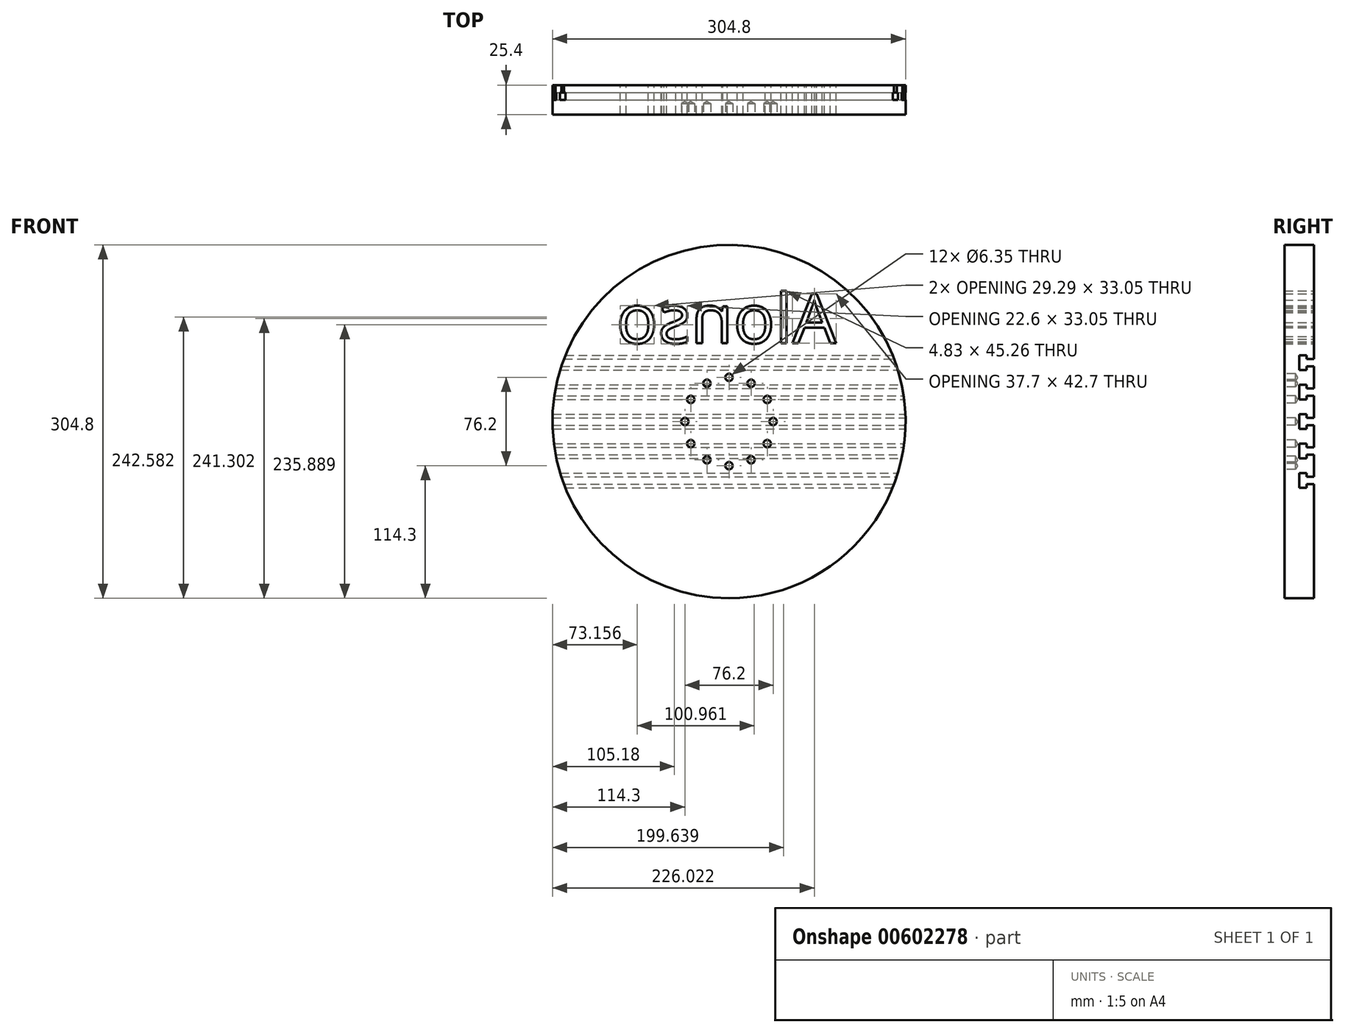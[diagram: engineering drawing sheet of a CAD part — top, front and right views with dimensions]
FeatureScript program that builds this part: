
annotation { "Feature Type Name" : "Feature", "Feature Type Description" : "" }
export const myFeature = defineFeature(function(context is Context, id is Id, definition is map)
    precondition{}
    {
        {
            var Q0;
            Q0=qCreatedBy(makeId("Front.planeOp"),FACE);
            var sketch = newSketch(context, id + "F0", { "sketchPlane" : qUnion([Q0])});
            skCircle(sketch, "E0", {"center": v(0, 0) * mm, "radius": 152.4 * mm});
            skSolve(sketch);
        }
        {
            var Q0;
            Q0 = qSketchRegion(id + "F0", true);
            extrude(context, id + "F1", {"entities" : qUnion([Q0]), "depth" : 25.4 * mm, "offsetDistance" : 25.4 * mm});
        }
        {
            var Q0;
            Q0=makeQuery(id+"F1.opExtrude","CAP_FACE",FACE,{"disambiguationData":[OSD([sQuery(id+"F0.wireOp",EDGE,"E0")])],"isStart":false});
            var sketch = newSketch(context, id + "F2", { "sketchPlane" : qUnion([Q0])});
            skCircle(sketch, "E1.0.0", {"center": v(0, 0) * mm, "radius": 152.4 * mm});
            skPoint(sketch, "E2", {"position": v(0, -38.1) * mm});
            skPoint(sketch, "E3.1.0", {"position": v(19.05, -33) * mm});
            skPoint(sketch, "E3.2.0", {"position": v(33, -19.05) * mm});
            skPoint(sketch, "E3.3.0", {"position": v(38.1, 0) * mm});
            skPoint(sketch, "E3.4.0", {"position": v(33, 19.05) * mm});
            skPoint(sketch, "E3.5.0", {"position": v(19.05, 33) * mm});
            skPoint(sketch, "E3.6.0", {"position": v(0, 38.1) * mm});
            skPoint(sketch, "E3.7.0", {"position": v(-19.05, 33) * mm});
            skPoint(sketch, "E3.8.0", {"position": v(-33, 19.05) * mm});
            skPoint(sketch, "E3.9.0", {"position": v(-38.1, 0) * mm});
            skPoint(sketch, "E3.10.0", {"position": v(-33, -19.05) * mm});
            skPoint(sketch, "E3.11.0", {"position": v(-19.05, -33) * mm});
            skSolve(sketch);
        }
        {
            var Q0;
            Q0=sQuery(id+"F2.wireOp",VERTEX,"E3.7.0");
            var Q1;
            Q1=sQuery(id+"F2.wireOp",VERTEX,"E3.6.0");
            var Q2;
            Q2=sQuery(id+"F2.wireOp",VERTEX,"E3.5.0");
            var Q3;
            Q3=sQuery(id+"F2.wireOp",VERTEX,"E3.4.0");
            var Q4;
            Q4=sQuery(id+"F2.wireOp",VERTEX,"E3.3.0");
            var Q5;
            Q5=sQuery(id+"F2.wireOp",VERTEX,"E3.2.0");
            var Q6;
            Q6=sQuery(id+"F2.wireOp",VERTEX,"E3.1.0");
            var Q7;
            Q7=sQuery(id+"F2.wireOp",VERTEX,"E2");
            var Q8;
            Q8=sQuery(id+"F2.wireOp",VERTEX,"E3.11.0");
            var Q9;
            Q9=sQuery(id+"F2.wireOp",VERTEX,"E3.10.0");
            var Q10;
            Q10=sQuery(id+"F2.wireOp",VERTEX,"E3.8.0");
            var Q11;
            Q11=sQuery(id+"F2.wireOp",VERTEX,"E3.9.0");
            var Q12;
            Q12=makeQuery(id+"F1.opExtrude","SWEPT_BODY",BODY,{"disambiguationData":[OSD([sQuery(id+"F0.wireOp",EDGE,"E0")])]});
            hole(context, id + "F3", {"style" : HoleStyle.SIMPLE, "endStyle" : HoleEndStyle.BLIND, "holeDiameter" : 6.35 * mm, "majorDiameter" : 6.35 * mm, "holeDepth" : 9.52 * mm, "isTappedThrough" : true, "tappedDepth" : 12.7 * mm, "tapClearance" : 3, "locations" : qUnion([Q0, Q1, Q2, Q3, Q4, Q5, Q6, Q7, Q8, Q9, Q10, Q11]), "scope" : qUnion([Q12])});
        }
        {
            var Q0;
            Q0=makeQuery(id+"F1.opExtrude","CAP_FACE",FACE,{"disambiguationData":[OSD([sQuery(id+"F0.wireOp",EDGE,"E0")])],"isStart":true});
            var sketch = newSketch(context, id + "F4", { "sketchPlane" : qUnion([Q0])});
            skSolve(sketch);
        }
        {
            var Q0;
            Q0=qCreatedBy(makeId("Right.planeOp"),FACE);
            cPlane(context, id + "F5", {"entities" : qUnion([Q0]), "cplaneType" : CPlaneType.OFFSET, "offset" : 152.4 * mm, "width" : 152.4 * mm, "height" : 152.4 * mm});
        }
        {
            var Q0;
            Q0=qCreatedBy(id+"F5.planeOp",FACE);
            var sketch = newSketch(context, id + "F6", { "sketchPlane" : qUnion([Q0])});
            skLineSegment(sketch, "E4.0", {"start": v(-25.4, -152.4) * mm, "end": v(-25.4, 152.4) * mm});
            skLineSegment(sketch, "E5.0", {"start": v(0, -152.4) * mm, "end": v(0, 152.4) * mm});
            skPoint(sketch, "E6", {"position": v(-25.4, 0) * mm});
            skPoint(sketch, "E7", {"position": v(0, 0) * mm});
            skPoint(sketch, "E8", {"position": v(0, 3.18) * mm});
            skPoint(sketch, "E9", {"position": v(0, -3.18) * mm});
            skPoint(sketch, "E10", {"position": v(-6.35, 3.17) * mm});
            skPoint(sketch, "E11", {"position": v(-6.35, -3.18) * mm});
            skLineSegment(sketch, "E12", {"start": v(0, 3.18) * mm, "end": v(-6.35, 3.17) * mm});
            skLineSegment(sketch, "E13", {"start": v(0, -3.18) * mm, "end": v(-6.35, -3.18) * mm});
            skPoint(sketch, "E14", {"position": v(-6.35, -6.35) * mm});
            skPoint(sketch, "E15", {"position": v(-6.35, 6.35) * mm});
            skPoint(sketch, "E16", {"position": v(-12.7, 6.35) * mm});
            skPoint(sketch, "E17", {"position": v(-12.7, -6.35) * mm});
            skLineSegment(sketch, "E18", {"start": v(-6.35, 3.17) * mm, "end": v(-6.35, 6.35) * mm});
            skLineSegment(sketch, "E19", {"start": v(-6.35, 6.35) * mm, "end": v(-12.7, 6.35) * mm});
            skLineSegment(sketch, "E20", {"start": v(-6.35, -3.18) * mm, "end": v(-6.35, -6.35) * mm});
            skLineSegment(sketch, "E21", {"start": v(-6.35, -6.35) * mm, "end": v(-12.7, -6.35) * mm});
            skLineSegment(sketch, "E22", {"start": v(-12.7, 6.35) * mm, "end": v(-12.7, -6.35) * mm});
            skPoint(sketch, "E23", {"position": v(0, 25.4) * mm});
            skPoint(sketch, "E24", {"position": v(0, 28.58) * mm});
            skPoint(sketch, "E25", {"position": v(0, 22.23) * mm});
            skPoint(sketch, "E26", {"position": v(-6.35, 28.58) * mm});
            skPoint(sketch, "E27", {"position": v(-6.35, 22.23) * mm});
            skPoint(sketch, "E28", {"position": v(-6.35, 19.05) * mm});
            skPoint(sketch, "E29", {"position": v(-6.35, 31.75) * mm});
            skPoint(sketch, "E30", {"position": v(-12.7, 19.05) * mm});
            skLineSegment(sketch, "E31", {"start": v(0, 22.23) * mm, "end": v(-6.35, 22.23) * mm});
            skLineSegment(sketch, "E32", {"start": v(-6.35, 22.23) * mm, "end": v(-6.35, 19.05) * mm});
            skLineSegment(sketch, "E33", {"start": v(-6.35, 19.05) * mm, "end": v(-12.7, 19.05) * mm});
            skLineSegment(sketch, "E34", {"start": v(-12.7, 19.05) * mm, "end": v(-12.7, 28.58) * mm});
            skLineSegment(sketch, "E35", {"start": v(0, 28.58) * mm, "end": v(-6.35, 28.58) * mm});
            skLineSegment(sketch, "E36", {"start": v(-6.35, 28.58) * mm, "end": v(-6.35, 31.75) * mm});
            skLineSegment(sketch, "E37", {"start": v(-6.35, 31.75) * mm, "end": v(-12.7, 31.75) * mm});
            skLineSegment(sketch, "E38", {"start": v(-12.7, 31.75) * mm, "end": v(-12.7, 28.58) * mm});
            skPoint(sketch, "E39", {"position": v(0, 50.8) * mm});
            skPoint(sketch, "E40", {"position": v(0, 53.98) * mm});
            skPoint(sketch, "E41", {"position": v(0, 47.63) * mm});
            skPoint(sketch, "E42", {"position": v(-6.35, 53.98) * mm});
            skPoint(sketch, "E43", {"position": v(-6.35, 47.63) * mm});
            skPoint(sketch, "E44", {"position": v(-6.35, 44.45) * mm});
            skPoint(sketch, "E45", {"position": v(-6.35, 57.15) * mm});
            skPoint(sketch, "E46", {"position": v(-12.7, 57.15) * mm});
            skPoint(sketch, "E47", {"position": v(-12.7, 44.45) * mm});
            skLineSegment(sketch, "E48", {"start": v(0, 47.63) * mm, "end": v(-6.35, 47.63) * mm});
            skLineSegment(sketch, "E49", {"start": v(-6.35, 47.63) * mm, "end": v(-6.35, 44.45) * mm});
            skLineSegment(sketch, "E50", {"start": v(-6.35, 44.45) * mm, "end": v(-12.7, 44.45) * mm});
            skLineSegment(sketch, "E51", {"start": v(-12.7, 44.45) * mm, "end": v(-12.7, 57.15) * mm});
            skLineSegment(sketch, "E52", {"start": v(-12.7, 57.15) * mm, "end": v(-6.35, 57.15) * mm});
            skLineSegment(sketch, "E53", {"start": v(-6.35, 57.15) * mm, "end": v(-6.35, 53.98) * mm});
            skLineSegment(sketch, "E54", {"start": v(-6.35, 53.98) * mm, "end": v(0, 53.98) * mm});
            skPoint(sketch, "E55", {"position": v(0, -25.4) * mm});
            skPoint(sketch, "E56", {"position": v(0, -22.23) * mm});
            skPoint(sketch, "E57", {"position": v(0, -28.58) * mm});
            skPoint(sketch, "E58", {"position": v(-6.35, -22.23) * mm});
            skPoint(sketch, "E59", {"position": v(-6.35, -28.58) * mm});
            skPoint(sketch, "E60", {"position": v(-6.35, -19.05) * mm});
            skPoint(sketch, "E61", {"position": v(-6.35, -31.75) * mm});
            skPoint(sketch, "E62", {"position": v(-12.7, -19.05) * mm});
            skPoint(sketch, "E63", {"position": v(-12.7, -31.75) * mm});
            skLineSegment(sketch, "E64", {"start": v(0, -22.23) * mm, "end": v(-6.35, -22.23) * mm});
            skLineSegment(sketch, "E65", {"start": v(-6.35, -22.23) * mm, "end": v(-6.35, -19.05) * mm});
            skLineSegment(sketch, "E66", {"start": v(-6.35, -19.05) * mm, "end": v(-12.7, -19.05) * mm});
            skLineSegment(sketch, "E67", {"start": v(-12.7, -19.05) * mm, "end": v(-12.7, -31.75) * mm});
            skLineSegment(sketch, "E68", {"start": v(-12.7, -31.75) * mm, "end": v(-6.35, -31.75) * mm});
            skLineSegment(sketch, "E69", {"start": v(-6.35, -31.75) * mm, "end": v(-6.35, -28.58) * mm});
            skLineSegment(sketch, "E70", {"start": v(-6.35, -28.58) * mm, "end": v(0, -28.58) * mm});
            skPoint(sketch, "E71", {"position": v(0, -50.8) * mm});
            skPoint(sketch, "E72", {"position": v(0, -47.63) * mm});
            skPoint(sketch, "E73", {"position": v(0, -53.98) * mm});
            skPoint(sketch, "E74", {"position": v(-6.35, -47.63) * mm});
            skPoint(sketch, "E75", {"position": v(-6.35, -53.98) * mm});
            skPoint(sketch, "E76", {"position": v(-6.35, -44.45) * mm});
            skPoint(sketch, "E77", {"position": v(-6.35, -57.15) * mm});
            skPoint(sketch, "E78", {"position": v(-12.7, -44.45) * mm});
            skPoint(sketch, "E79", {"position": v(-12.7, -57.15) * mm});
            skLineSegment(sketch, "E80", {"start": v(0, -47.63) * mm, "end": v(-6.35, -47.63) * mm});
            skLineSegment(sketch, "E81", {"start": v(-6.35, -47.63) * mm, "end": v(-6.35, -44.45) * mm});
            skLineSegment(sketch, "E82", {"start": v(-6.35, -44.45) * mm, "end": v(-12.7, -44.45) * mm});
            skLineSegment(sketch, "E83", {"start": v(-12.7, -44.45) * mm, "end": v(-12.7, -57.15) * mm});
            skLineSegment(sketch, "E84", {"start": v(-12.7, -57.15) * mm, "end": v(-6.35, -57.15) * mm});
            skLineSegment(sketch, "E85", {"start": v(-6.35, -57.15) * mm, "end": v(-6.35, -53.98) * mm});
            skLineSegment(sketch, "E86", {"start": v(-6.35, -53.98) * mm, "end": v(0, -53.98) * mm});
            skSolve(sketch);
        }
        {
            var Q0;
            {var subQ1=sQuery(id+"F6.wireOp",EDGE,"E12");Q0=makeQuery(id+"F6.imprint","IMPRINT",FACE,{"disambiguationData":[TD([[makeQuery(id+"F6.imprint","IMPRINT",EDGE,{"derivedFrom":subQ1}),1.0]])]});}
            var Q1;
            {var subQ0=sQuery(id+"F6.wireOp",EDGE,"E80");Q1=makeQuery(id+"F6.imprint","IMPRINT",FACE,{"disambiguationData":[TD([[makeQuery(id+"F6.imprint","IMPRINT",EDGE,{"derivedFrom":subQ0}),1.0]])]});}
            var Q2;
            {var subQ0=sQuery(id+"F6.wireOp",EDGE,"E64");Q2=makeQuery(id+"F6.imprint","IMPRINT",FACE,{"disambiguationData":[TD([[makeQuery(id+"F6.imprint","IMPRINT",EDGE,{"derivedFrom":subQ0}),1.0]])]});}
            var Q3;
            {var subQ0=sQuery(id+"F6.wireOp",EDGE,"E31");Q3=makeQuery(id+"F6.imprint","IMPRINT",FACE,{"disambiguationData":[TD([[makeQuery(id+"F6.imprint","IMPRINT",EDGE,{"derivedFrom":subQ0}),-1.0]])]});}
            var Q4;
            {var subQ0=sQuery(id+"F6.wireOp",EDGE,"E48");Q4=makeQuery(id+"F6.imprint","IMPRINT",FACE,{"disambiguationData":[TD([[makeQuery(id+"F6.imprint","IMPRINT",EDGE,{"derivedFrom":subQ0}),-1.0]])]});}
            var Q5;
            Q5=makeQuery(id+"F1.opExtrude","SWEPT_FACE",FACE,{"disambiguationData":[OSD([sQuery(id+"F0.wireOp",EDGE,"E0")])]});
            extrude(context, id + "F7", {"entities" : qUnion([Q0, Q1, Q2, Q3, Q4]), "operationType" : NewBodyOperationType.REMOVE, "oppositeDirection" : true, "depth" : 304.8 * mm, "endBoundEntityFace" : qUnion([Q5]), "offsetDistance" : 25.4 * mm});
        }
        {
            var Q0;
            Q0=makeQuery(id+"F4.imprint","IMPRINT",FACE,{"disambiguationData":[TD([[makeQuery(id+"F4.imprint","IMPRINT",EDGE,{"derivedFrom":makeQuery(id+"F1.opExtrude","CAP_EDGE",EDGE,{"disambiguationData":[OSD([sQuery(id+"F0.wireOp",EDGE,"E0")])],"isStart":true})}),-1.0]])]});
            var sketch = newSketch(context, id + "F8", { "sketchPlane" : qUnion([Q0])});
            skText(sketch, "E87", { "text": "Alonso", "fontName": "OpenSans-Regular.ttf"});
            const initialGuessF8  = {"E87": [-0.09247, 0.06755, 1, 0, 0.04289]};
            skSetInitialGuess(sketch, initialGuessF8);
            skSolve(sketch);
        }
        {
            var Q0;
            Q0 = qSketchRegion(id + "F8", true);
            extrude(context, id + "F9", {"entities" : qUnion([Q0]), "operationType" : NewBodyOperationType.REMOVE, "oppositeDirection" : true, "depth" : 25.4 * mm, "offsetDistance" : 25.4 * mm});
        }
    });
